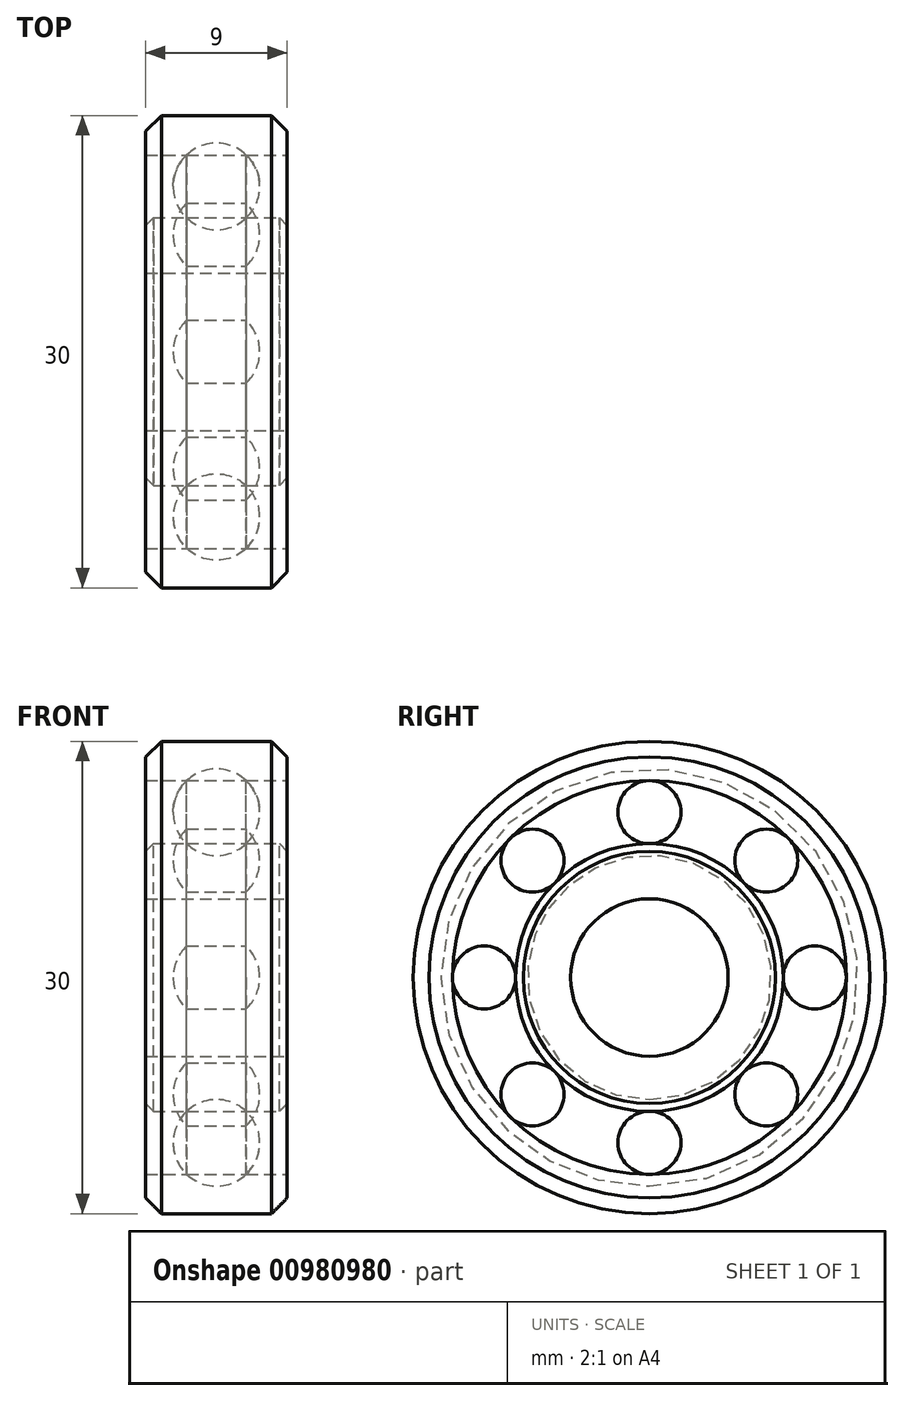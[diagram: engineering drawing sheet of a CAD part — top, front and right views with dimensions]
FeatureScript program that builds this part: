
annotation { "Feature Type Name" : "Feature", "Feature Type Description" : "" }
export const myFeature = defineFeature(function(context is Context, id is Id, definition is map)
    precondition{}
    {
        {
            var Q0;
            Q0=qCreatedBy(makeId("Right.planeOp"),FACE);
            var sketch = newSketch(context, id + "F0", { "sketchPlane" : qUnion([Q0])});
            skLineSegment(sketch, "E0", {"start": v(-11.44, 0) * mm, "end": v(12.35, 0) * mm, "construction": true});
            skCircle(sketch, "E1", {"center": v(0, 10.5) * mm, "radius": 2.75 * mm});
            skLineSegment(sketch, "E2.bottom", {"start": v(-4.5, 5) * mm, "end": v(4.5, 5) * mm});
            skLineSegment(sketch, "E2.top", {"start": v(-4.5, 8.5) * mm, "end": v(4.5, 8.5) * mm});
            skLineSegment(sketch, "E2.left", {"start": v(-4.5, 5) * mm, "end": v(-4.5, 8.5) * mm});
            skLineSegment(sketch, "E2.right", {"start": v(4.5, 5) * mm, "end": v(4.5, 8.5) * mm});
            skLineSegment(sketch, "E3.bottom", {"start": v(-4.5, 12.5) * mm, "end": v(4.5, 12.5) * mm});
            skLineSegment(sketch, "E3.top", {"start": v(-4.5, 15) * mm, "end": v(4.5, 15) * mm});
            skLineSegment(sketch, "E3.left", {"start": v(-4.5, 12.5) * mm, "end": v(-4.5, 15) * mm});
            skLineSegment(sketch, "E3.right", {"start": v(4.5, 12.5) * mm, "end": v(4.5, 15) * mm});
            skLineSegment(sketch, "E4", {"start": v(0, 0) * mm, "end": v(0, 30.94) * mm, "construction": true});
            skPoint(sketch, "E5", {"position": v(0, 8.5) * mm});
            skLineSegment(sketch, "E6", {"start": v(-6.72, 10.5) * mm, "end": v(10, 10.5) * mm, "construction": true});
            skLineSegment(sketch, "E7", {"start": v(-2.75, 10.5) * mm, "end": v(2.75, 10.5) * mm});
            skSolve(sketch);
        }
        {
            var Q0;
            Q0=makeQuery(id+"F0.imprint","IMPRINT",FACE,{"disambiguationData":[TD([[makeQuery(id+"F0.imprint","IMPRINT",EDGE,{"derivedFrom":sQuery(id+"F0.wireOp",EDGE,"E2.bottom")}),1.0]])]});
            var Q1;
            Q1=makeQuery(id+"F0.imprint","IMPRINT",FACE,{"disambiguationData":[TD([[makeQuery(id+"F0.imprint","IMPRINT",EDGE,{"derivedFrom":sQuery(id+"F0.wireOp",EDGE,"E3.top")}),-1.0]])]});
            var Q2;
            Q2=sQuery(id+"F0.wireOp",EDGE,"E0");
            revolve(context, id + "F1", {"surfaceOperationType" : NewSurfaceOperationType.NEW, "entities" : qUnion([Q0, Q1]), "axis" : qUnion([Q2]), "revolveType" : RevolveType.FULL});
        }
        {
            var Q0;
            {var subQ0=sQuery(id+"F0.wireOp",EDGE,"E7");Q0=makeQuery(id+"F0.imprint","IMPRINT",FACE,{"disambiguationData":[TD([[makeQuery(id+"F0.imprint","IMPRINT",EDGE,{"derivedFrom":subQ0}),1.0]])]});}
            var Q1;
            {var subQ0=sQuery(id+"F0.wireOp",EDGE,"E3.bottom");var subQ1=sQuery(id+"F0.wireOp",EDGE,"E1");var subQ2=makeQuery(id+"F0.imprint","INTERSECT",VERTEX,{"disambiguationData":[OD(0.0)],"derivedFrom":[subQ1,subQ0]});Q1=makeQuery(id+"F0.imprint","IMPRINT",FACE,{"disambiguationData":[TD([[makeQuery(id+"F0.imprint","IMPRINT",EDGE,{"disambiguationData":[TD([[subQ2,-1.0]])],"derivedFrom":subQ1}),1.0]])]});}
            var Q2;
            Q2=sQuery(id+"F0.wireOp",EDGE,"E6");
            revolve(context, id + "F2", {"surfaceOperationType" : NewSurfaceOperationType.NEW, "entities" : qUnion([Q0, Q1]), "axis" : qUnion([Q2]), "revolveType" : RevolveType.FULL});
        }
        {
            var Q0;
            Q0=makeQuery(id+"F2.opRevolve","SWEPT_BODY",BODY,{"disambiguationData":[OSD([sQuery(id+"F0.wireOp",EDGE,"E1"),sQuery(id+"F0.wireOp",EDGE,"E7")])]});
            var Q1;
            Q1=sQuery(id+"F0.wireOp",EDGE,"E0");
            circularPattern(context, id + "F3", {"entities" : qUnion([Q0]), "axis" : qUnion([Q1]), "angle" : 360 * degree, "instanceCount" : 8, "equalSpace" : true});
        }
        {
            var Q0;
            Q0=makeQuery(id+"F1.opRevolve","SWEPT_EDGE",EDGE,{"disambiguationData":[OSD([sQuery(id+"F0.wireOp",EDGE,"E3.top"),sQuery(id+"F0.wireOp",EDGE,"E3.left")])]});
            var Q1;
            Q1=makeQuery(id+"F1.opRevolve","SWEPT_EDGE",EDGE,{"disambiguationData":[OSD([sQuery(id+"F0.wireOp",EDGE,"E3.top"),sQuery(id+"F0.wireOp",EDGE,"E3.right")])]});
            chamfer(context, id + "F4", {"entities" : qUnion([Q0, Q1]), "width" : 1 * mm, "tangentPropagation" : true});
        }
        {
            var Q0;
            Q0=makeQuery(id+"F1.opRevolve","SWEPT_EDGE",EDGE,{"disambiguationData":[OSD([sQuery(id+"F0.wireOp",EDGE,"E2.top"),sQuery(id+"F0.wireOp",EDGE,"E2.left")])]});
            var Q1;
            Q1=makeQuery(id+"F1.opRevolve","SWEPT_EDGE",EDGE,{"disambiguationData":[OSD([sQuery(id+"F0.wireOp",EDGE,"E2.top"),sQuery(id+"F0.wireOp",EDGE,"E2.right")])]});
            chamfer(context, id + "F5", {"entities" : qUnion([Q0, Q1]), "width" : 0.5 * mm, "tangentPropagation" : true});
        }
        {
            var Q0;
            Q0=makeQuery(id+"F1.opRevolve","SWEPT_BODY",BODY,{"disambiguationData":[OSD([sQuery(id+"F0.wireOp",EDGE,"E1"),sQuery(id+"F0.wireOp",EDGE,"E3.bottom"),sQuery(id+"F0.wireOp",EDGE,"E3.top"),sQuery(id+"F0.wireOp",EDGE,"E3.left"),sQuery(id+"F0.wireOp",EDGE,"E3.right")])]});
            var Q1;
            Q1=makeQuery(id+"F3.opPattern","COPY",BODY,{"derivedFrom":makeQuery(id+"F2.opRevolve","SWEPT_BODY",BODY,{"disambiguationData":[OSD([sQuery(id+"F0.wireOp",EDGE,"E1"),sQuery(id+"F0.wireOp",EDGE,"E7")])]}),"instanceName":"3"});
            var Q2;
            Q2=makeQuery(id+"F3.opPattern","COPY",BODY,{"derivedFrom":makeQuery(id+"F2.opRevolve","SWEPT_BODY",BODY,{"disambiguationData":[OSD([sQuery(id+"F0.wireOp",EDGE,"E1"),sQuery(id+"F0.wireOp",EDGE,"E7")])]}),"instanceName":"2"});
            var Q3;
            Q3=makeQuery(id+"F3.opPattern","COPY",BODY,{"derivedFrom":makeQuery(id+"F2.opRevolve","SWEPT_BODY",BODY,{"disambiguationData":[OSD([sQuery(id+"F0.wireOp",EDGE,"E1"),sQuery(id+"F0.wireOp",EDGE,"E7")])]}),"instanceName":"1"});
            var Q4;
            Q4=makeQuery(id+"F1.opRevolve","SWEPT_BODY",BODY,{"disambiguationData":[OSD([sQuery(id+"F0.wireOp",EDGE,"E1"),sQuery(id+"F0.wireOp",EDGE,"E2.bottom"),sQuery(id+"F0.wireOp",EDGE,"E2.top"),sQuery(id+"F0.wireOp",EDGE,"E2.left"),sQuery(id+"F0.wireOp",EDGE,"E2.right")])]});
            var Q5;
            Q5=makeQuery(id+"F3.opPattern","COPY",BODY,{"derivedFrom":makeQuery(id+"F2.opRevolve","SWEPT_BODY",BODY,{"disambiguationData":[OSD([sQuery(id+"F0.wireOp",EDGE,"E1"),sQuery(id+"F0.wireOp",EDGE,"E7")])]}),"instanceName":"4"});
            var Q6;
            Q6=makeQuery(id+"F2.opRevolve","SWEPT_BODY",BODY,{"disambiguationData":[OSD([sQuery(id+"F0.wireOp",EDGE,"E1"),sQuery(id+"F0.wireOp",EDGE,"E7")])]});
            var Q7;
            Q7=makeQuery(id+"F3.opPattern","COPY",BODY,{"derivedFrom":makeQuery(id+"F2.opRevolve","SWEPT_BODY",BODY,{"disambiguationData":[OSD([sQuery(id+"F0.wireOp",EDGE,"E1"),sQuery(id+"F0.wireOp",EDGE,"E7")])]}),"instanceName":"6"});
            var Q8;
            Q8=makeQuery(id+"F3.opPattern","COPY",BODY,{"derivedFrom":makeQuery(id+"F2.opRevolve","SWEPT_BODY",BODY,{"disambiguationData":[OSD([sQuery(id+"F0.wireOp",EDGE,"E1"),sQuery(id+"F0.wireOp",EDGE,"E7")])]}),"instanceName":"5"});
            var Q9;
            Q9=makeQuery(id+"F3.opPattern","COPY",BODY,{"derivedFrom":makeQuery(id+"F2.opRevolve","SWEPT_BODY",BODY,{"disambiguationData":[OSD([sQuery(id+"F0.wireOp",EDGE,"E1"),sQuery(id+"F0.wireOp",EDGE,"E7")])]}),"instanceName":"7"});
            var Q10;
            Q10=sQuery(id+"F0.wireOp",EDGE,"E4");
            transform(context, id + "F6", {"entities" : qUnion([Q0, Q1, Q2, Q3, Q4, Q5, Q6, Q7, Q8, Q9]), "transformType" : TransformType.ROTATION, "transformAxis" : qUnion([Q10]), "angle" : 90 * degree, "makeCopy" : false});
        }
    });
